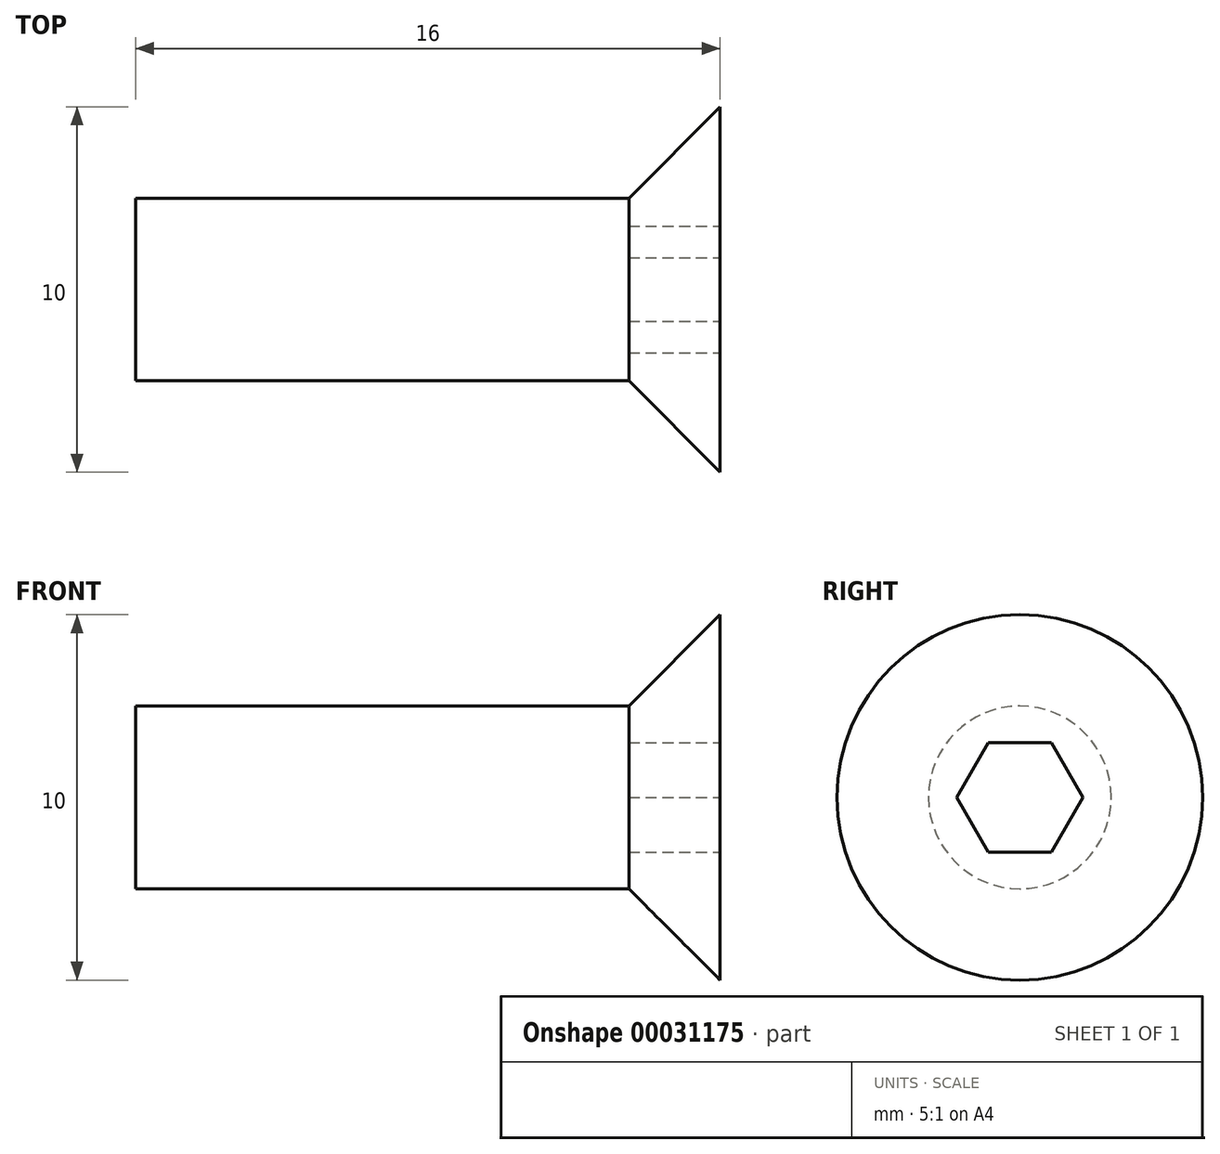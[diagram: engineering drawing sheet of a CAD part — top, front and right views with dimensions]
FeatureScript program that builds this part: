
annotation { "Feature Type Name" : "Feature", "Feature Type Description" : "" }
export const myFeature = defineFeature(function(context is Context, id is Id, definition is map)
    precondition{}
    {
        {
            var Q0;
            Q0=qCreatedBy(makeId("Front.planeOp"),FACE);
            var sketch = newSketch(context, id + "F0", { "sketchPlane" : qUnion([Q0])});
            skLineSegment(sketch, "E0", {"start": v(0, 0) * mm, "end": v(0, 2.5) * mm});
            skLineSegment(sketch, "E1", {"start": v(0, 2.5) * mm, "end": v(13.5, 2.5) * mm});
            skLineSegment(sketch, "E2", {"start": v(13.5, 2.5) * mm, "end": v(16, 5) * mm});
            skLineSegment(sketch, "E3", {"start": v(16, 5) * mm, "end": v(16, 0) * mm});
            skLineSegment(sketch, "E4", {"start": v(16, 0) * mm, "end": v(0, 0) * mm});
            skSolve(sketch);
        }
        {
            var Q0;
            Q0 = qSketchRegion(id + "F0", true);
            var Q1;
            Q1=sQuery(id+"F0.wireOp",EDGE,"E4");
            revolve(context, id + "F1", {"entities" : qUnion([Q0]), "axis" : qUnion([Q1]), "revolveType" : RevolveType.FULL});
        }
        {
            var Q0;
            Q0=makeQuery(id+"F1.opRevolve","SWEPT_FACE",FACE,{"disambiguationData":[OSD([sQuery(id+"F0.wireOp",EDGE,"E3")])]});
            var sketch = newSketch(context, id + "F2", { "sketchPlane" : qUnion([Q0])});
            skCircle(sketch, "E5.cCircle", {"center": v(0, 0) * mm, "radius": 1.5 * mm, "construction": true});
            skLineSegment(sketch, "E5.0", {"start": v(-0.87, 1.5) * mm, "end": v(0.87, 1.5) * mm});
            skLineSegment(sketch, "E5.1", {"start": v(0.87, 1.5) * mm, "end": v(1.73, 0) * mm});
            skLineSegment(sketch, "E5.2", {"start": v(1.73, 0) * mm, "end": v(0.87, -1.5) * mm});
            skLineSegment(sketch, "E5.3", {"start": v(0.87, -1.5) * mm, "end": v(-0.87, -1.5) * mm});
            skLineSegment(sketch, "E5.4", {"start": v(-0.87, -1.5) * mm, "end": v(-1.73, 0) * mm});
            skLineSegment(sketch, "E5.5", {"start": v(-1.73, 0) * mm, "end": v(-0.87, 1.5) * mm});
            skPoint(sketch, "E5.0.midPoint", {"position": v(0, 1.5) * mm});
            skSolve(sketch);
        }
        {
            var Q0;
            Q0 = qSketchRegion(id + "F2", true);
            extrude(context, id + "F3", {"entities" : qUnion([Q0]), "operationType" : NewBodyOperationType.REMOVE, "oppositeDirection" : true, "depth" : 2.5 * mm});
        }
    });
